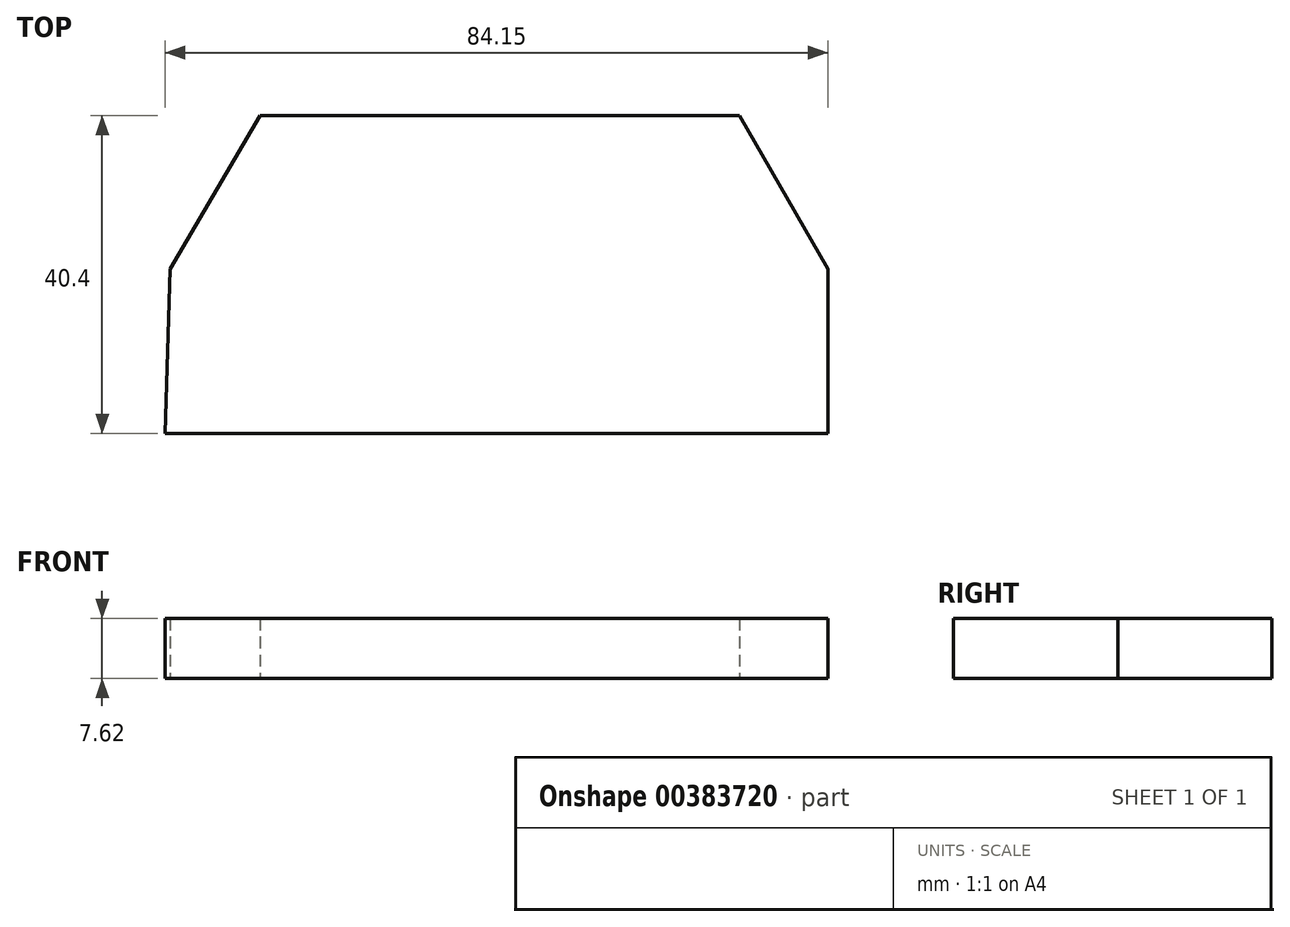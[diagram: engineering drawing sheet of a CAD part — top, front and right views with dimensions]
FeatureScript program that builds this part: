
annotation { "Feature Type Name" : "Feature", "Feature Type Description" : "" }
export const myFeature = defineFeature(function(context is Context, id is Id, definition is map)
    precondition{}
    {
        {
            var Q0;
            Q0=qCreatedBy(makeId("Top.planeOp"),FACE);
            var sketch = newSketch(context, id + "F0", { "sketchPlane" : qUnion([Q0])});
            skLineSegment(sketch, "E0", {"start": v(0, 0) * mm, "end": v(-45.72, 0) * mm});
            skLineSegment(sketch, "E1", {"start": v(0, 0) * mm, "end": v(38.43, 0) * mm});
            skLineSegment(sketch, "E2", {"start": v(38.43, 0) * mm, "end": v(38.43, 20.89) * mm});
            skLineSegment(sketch, "E3", {"start": v(38.43, 20.89) * mm, "end": v(27.2, 40.4) * mm});
            skLineSegment(sketch, "E4", {"start": v(-45.72, 0) * mm, "end": v(-45.13, 20.89) * mm});
            skLineSegment(sketch, "E5", {"start": v(-45.13, 20.89) * mm, "end": v(-33.7, 40.4) * mm});
            skLineSegment(sketch, "E6", {"start": v(27.2, 40.4) * mm, "end": v(-33.7, 40.4) * mm});
            skSolve(sketch);
        }
        {
            var Q0;
            Q0 = qSketchRegion(id + "F0", true);
            extrude(context, id + "F1", {"entities" : qUnion([Q0]), "depth" : 7.62 * mm});
        }
    });
